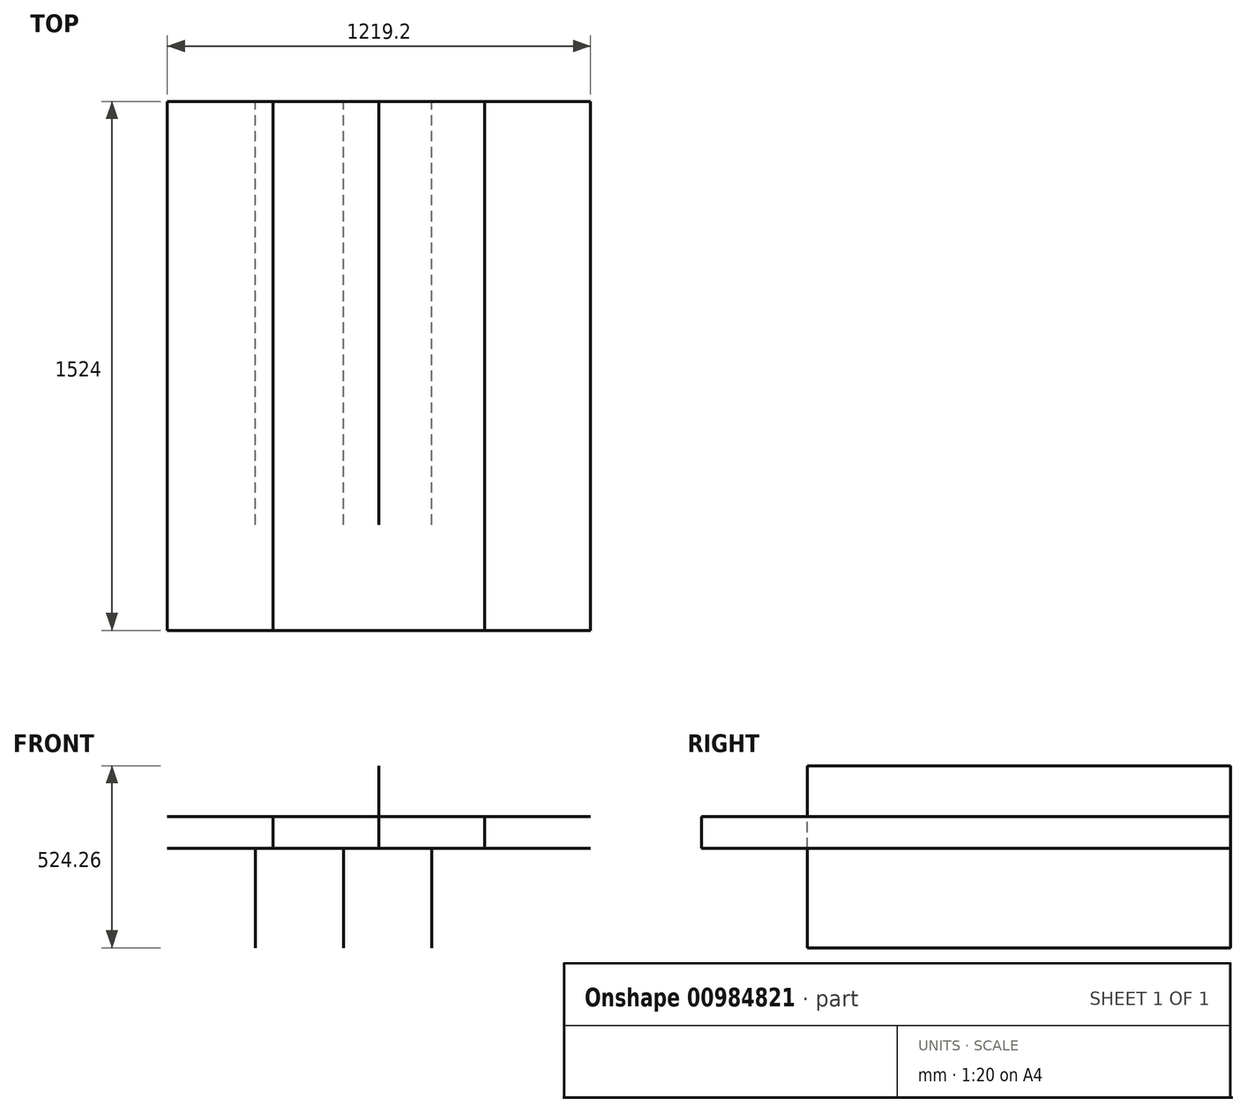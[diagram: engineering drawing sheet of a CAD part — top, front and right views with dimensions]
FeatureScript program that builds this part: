
annotation { "Feature Type Name" : "Feature", "Feature Type Description" : "" }
export const myFeature = defineFeature(function(context is Context, id is Id, definition is map)
    precondition{}
    {
        {
            var Q0;
            Q0=qCreatedBy(makeId("Front.planeOp"),FACE);
            var sketch = newSketch(context, id + "F0", { "sketchPlane" : qUnion([Q0])});
            skLineSegment(sketch, "E0.bottom", {"start": v(0, 0) * mm, "end": v(1219.2, 0) * mm});
            skLineSegment(sketch, "E0.top", {"start": v(0, 533.4) * mm, "end": v(1219.2, 533.4) * mm});
            skLineSegment(sketch, "E0.left", {"start": v(0, 0) * mm, "end": v(0, 533.4) * mm});
            skLineSegment(sketch, "E0.right", {"start": v(1219.2, 0) * mm, "end": v(1219.2, 533.4) * mm});
            skLineSegment(sketch, "E1", {"start": v(0, 286.51) * mm, "end": v(1219.2, 286.51) * mm});
            skLineSegment(sketch, "E2", {"start": v(0, 377.95) * mm, "end": v(1219.2, 377.95) * mm});
            skLineSegment(sketch, "E3", {"start": v(254, 0) * mm, "end": v(254, 286.51) * mm});
            skLineSegment(sketch, "E4", {"start": v(508, 0) * mm, "end": v(508, 286.51) * mm});
            skLineSegment(sketch, "E5", {"start": v(762, 0) * mm, "end": v(762, 286.51) * mm});
            skLineSegment(sketch, "E6", {"start": v(304.8, 377.95) * mm, "end": v(304.8, 286.51) * mm});
            skLineSegment(sketch, "E7", {"start": v(609.6, 377.95) * mm, "end": v(609.6, 286.51) * mm});
            skLineSegment(sketch, "E8", {"start": v(914.4, 377.95) * mm, "end": v(914.4, 286.51) * mm});
            skLineSegment(sketch, "E9", {"start": v(609.6, 377.95) * mm, "end": v(609.6, 524.26) * mm});
            skSolve(sketch);
        }
        {
            var Q0;
            Q0=sQuery(id+"F0.wireOp",EDGE,"E3");
            var Q1;
            Q1=sQuery(id+"F0.wireOp",EDGE,"E4");
            var Q2;
            Q2=sQuery(id+"F0.wireOp",EDGE,"E5");
            extrude(context, id + "F1", {"bodyType" : ToolBodyType.SURFACE, "surfaceEntities" : qUnion([Q0, Q1, Q2]), "oppositeDirection" : true, "depth" : 1219.2 * mm, "offsetDistance" : 30.48 * mm});
        }
        {
            var Q0;
            Q0=sQuery(id+"F0.wireOp",EDGE,"E1");
            extrude(context, id + "F2", {"bodyType" : ToolBodyType.SURFACE, "surfaceEntities" : qUnion([Q0]), "oppositeDirection" : true, "depth" : 1219.2 * mm, "offsetDistance" : 30.48 * mm, "hasSecondDirection" : true, "secondDirectionOppositeDirection" : false, "secondDirectionDepth" : 304.8 * mm});
        }
        {
            var Q0;
            Q0=sQuery(id+"F0.wireOp",EDGE,"E6");
            var Q1;
            Q1=sQuery(id+"F0.wireOp",EDGE,"E8");
            extrude(context, id + "F3", {"bodyType" : ToolBodyType.SURFACE, "surfaceEntities" : qUnion([Q0, Q1]), "oppositeDirection" : true, "depth" : 1219.2 * mm, "offsetDistance" : 30.48 * mm, "hasSecondDirection" : true, "secondDirectionOppositeDirection" : false, "secondDirectionDepth" : 304.8 * mm});
        }
        {
            var Q0;
            Q0=sQuery(id+"F0.wireOp",EDGE,"E2");
            extrude(context, id + "F4", {"bodyType" : ToolBodyType.SURFACE, "surfaceEntities" : qUnion([Q0]), "oppositeDirection" : true, "depth" : 1219.2 * mm, "offsetDistance" : 30.48 * mm, "hasSecondDirection" : true, "secondDirectionOppositeDirection" : false, "secondDirectionDepth" : 304.8 * mm});
        }
        {
            var Q0;
            Q0=sQuery(id+"F0.wireOp",EDGE,"E9");
            var Q1;
            Q1=sQuery(id+"F0.wireOp",EDGE,"E7");
            extrude(context, id + "F5", {"bodyType" : ToolBodyType.SURFACE, "surfaceEntities" : qUnion([Q0, Q1]), "oppositeDirection" : true, "depth" : 1219.2 * mm, "offsetDistance" : 30.48 * mm});
        }
    });
